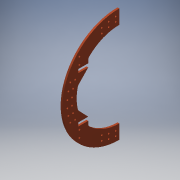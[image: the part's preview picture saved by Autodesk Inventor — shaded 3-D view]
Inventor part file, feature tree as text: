
AUTODESK INVENTOR PART (.ipt)
format: ipt  version: 2016 (Build 200138000, 138)  size: 284,160 bytes
history: native  units: in
note: dims shown in document units (in); Inventor stores cm internally (conversion verified against a paired STEP export)
features: reference x10, sketch x5, extrude x4, hole x2
ambient origin geometry x8: Origin, YZ Plane, XZ Plane, XY Plane, X Axis, Y Axis, Z Axis, Center Point
bodies: Solid1 (feature_tree)
feature tree (21):
  sketch  "Sketch1"  dims[d0=16.0in d2=12.0in]
  extrude  "Extrusion1"  Depth=12.0in
  hole  "Hole1"  [1 undecoded]
  hole  "Hole4"  [1 undecoded]
  extrude  "Extrusion3"  Depth=0.5in
  extrude  "Extrusion4"  Depth=0.25in
  extrude  "Extrusion5"  TaperAngle=45.0deg  [1 undecoded]
  sketch  "Sketch4"  dims[d3=14.6in d5=2.0in]
  reference  "Reference7"
  reference  "Reference8"
  sketch  "Sketch5"  dims[d6=1.0in d7=1.0in]
  reference  "Reference9"
  reference  "Reference10"
  reference  "Reference11"
  sketch  "Sketch6"  dims[d8=0.5in d9=0.5in]
  reference  "Reference12"
  reference  "Reference13"
  sketch  "Sketch7"  dims[d10=1.0in d11=1.0in d12=45.0deg d13=45.0deg d14=0.25in d15=0.0in d16=0.26in d17=0.75in d18=0.375in d19=0.25in d20=0.5635in d21=1.0in d22=0.8108in d37=0.26in d38=0.75in d39=0.375in d40=0.25in d41=0.5635in d42=1.0in d43=0.8108in d46=1.0in d47=0.0in d48=0.25in d49=0.0in d50=0.25in d51=0.0in]
  reference  "Reference14"
  reference  "Reference15"
  reference  "Reference16"
note: 3 required parameter values undecoded (feature->parameter linkage not recoverable at this tier; creation-order binding heuristic only, values carry confidence <= 0.55)
